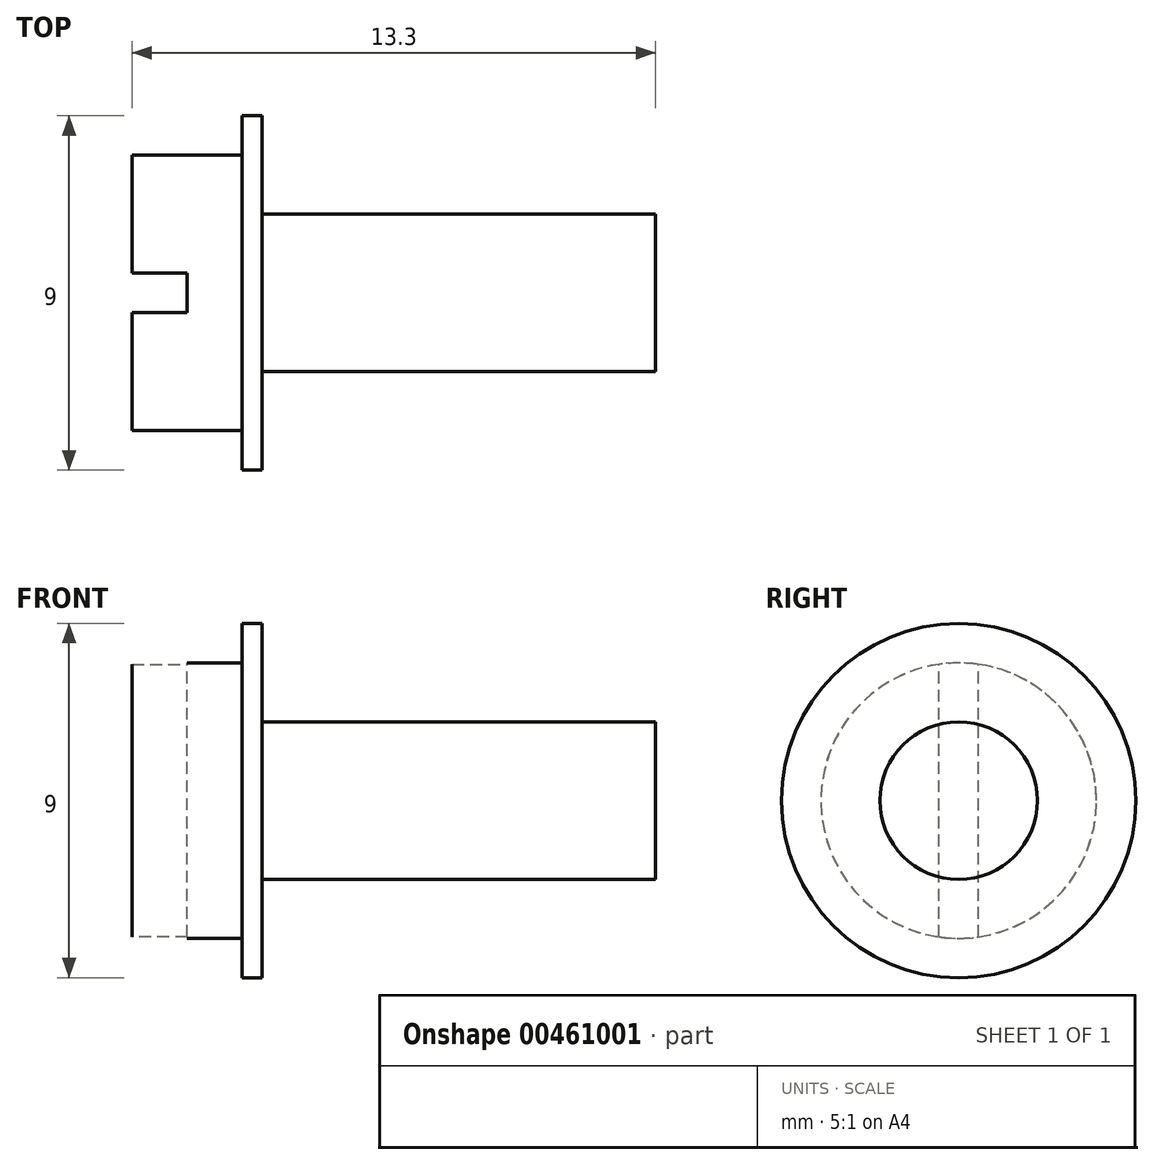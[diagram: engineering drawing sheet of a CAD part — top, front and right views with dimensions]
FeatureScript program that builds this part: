
annotation { "Feature Type Name" : "Feature", "Feature Type Description" : "" }
export const myFeature = defineFeature(function(context is Context, id is Id, definition is map)
    precondition{}
    {
        {
            var Q0;
            Q0=qCreatedBy(makeId("Front.planeOp"),FACE);
            var sketch = newSketch(context, id + "F0", { "sketchPlane" : qUnion([Q0])});
            skLineSegment(sketch, "E0", {"start": v(0, 0) * mm, "end": v(0, 3.5) * mm});
            skLineSegment(sketch, "E1", {"start": v(0, 3.5) * mm, "end": v(2.8, 3.5) * mm});
            skLineSegment(sketch, "E2", {"start": v(2.8, 3.5) * mm, "end": v(2.8, 4.5) * mm});
            skLineSegment(sketch, "E3", {"start": v(2.8, 4.5) * mm, "end": v(3.3, 4.5) * mm});
            skLineSegment(sketch, "E4", {"start": v(3.3, 4.5) * mm, "end": v(3.3, 3.5) * mm});
            skLineSegment(sketch, "E5", {"start": v(3.3, 3.5) * mm, "end": v(3.3, 2) * mm});
            skLineSegment(sketch, "E6", {"start": v(3.3, 2) * mm, "end": v(13.3, 2) * mm});
            skLineSegment(sketch, "E7", {"start": v(13.3, 2) * mm, "end": v(13.3, 0) * mm});
            skLineSegment(sketch, "E8", {"start": v(13.3, 0) * mm, "end": v(0, 0) * mm});
            skSolve(sketch);
        }
        {
            var Q0;
            Q0 = qSketchRegion(id + "F0", true);
            var Q1;
            Q1=sQuery(id+"F0.wireOp",EDGE,"E8");
            revolve(context, id + "F1", {"entities" : qUnion([Q0]), "axis" : qUnion([Q1]), "revolveType" : RevolveType.FULL});
        }
        {
            var Q0;
            Q0=makeQuery(id+"F1.opRevolve","SWEPT_FACE",FACE,{"disambiguationData":[OSD([sQuery(id+"F0.wireOp",EDGE,"E0")])]});
            var sketch = newSketch(context, id + "F2", { "sketchPlane" : qUnion([Q0])});
            skLineSegment(sketch, "E9.left", {"start": v(0.5, -3.46) * mm, "end": v(0.5, 3.46) * mm});
            skLineSegment(sketch, "E9.right", {"start": v(-0.5, -3.46) * mm, "end": v(-0.5, 3.46) * mm});
            skPoint(sketch, "E9.middle", {"position": v(0, 0) * mm});
            skArc(sketch, "E10", {"start": v(-0.5, -3.46) * mm, "mid": v(0, -3.5) * mm, "end": v(0.5, -3.46) * mm});
            skArc(sketch, "E11.trimOffspring", {"start": v(0.5, 3.46) * mm, "mid": v(0, 3.5) * mm, "end": v(-0.5, 3.46) * mm});
            skSolve(sketch);
        }
        {
            var Q0;
            Q0 = qSketchRegion(id + "F2", true);
            extrude(context, id + "F3", {"entities" : qUnion([Q0]), "operationType" : NewBodyOperationType.REMOVE, "oppositeDirection" : true, "depth" : 1.4 * mm});
        }
    });
